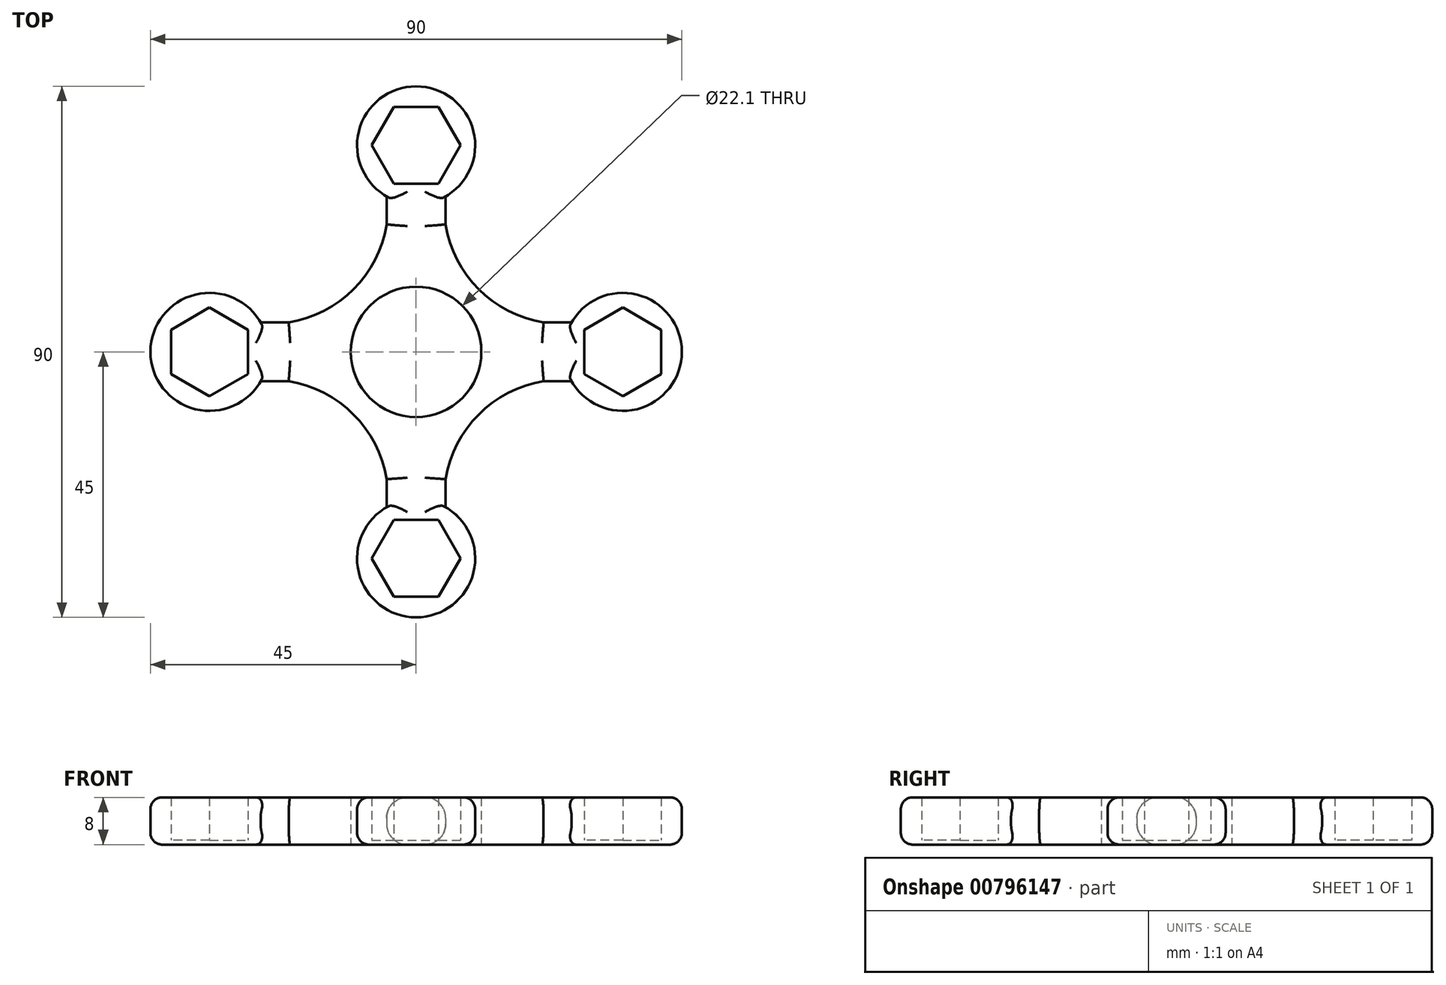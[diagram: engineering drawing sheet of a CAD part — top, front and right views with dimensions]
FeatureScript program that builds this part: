
annotation { "Feature Type Name" : "Feature", "Feature Type Description" : "" }
export const myFeature = defineFeature(function(context is Context, id is Id, definition is map)
    precondition{}
    {
        {
            var Q0;
            Q0=qCreatedBy(makeId("Top.planeOp"),FACE);
            var sketch = newSketch(context, id + "F0", { "sketchPlane" : qUnion([Q0])});
            skCircle(sketch, "E0", {"center": v(0, 0) * mm, "radius": 11.05 * mm});
            skCircle(sketch, "E1", {"center": v(0, 0) * mm, "radius": 35 * mm, "construction": true});
            skPoint(sketch, "E2", {"position": v(-35, 0) * mm});
            skPoint(sketch, "E3", {"position": v(35, 0) * mm});
            skPoint(sketch, "E4", {"position": v(0, 35) * mm});
            skPoint(sketch, "E5", {"position": v(0, -35) * mm});
            skCircle(sketch, "E6.cCircle", {"center": v(-35, 0) * mm, "radius": 6.5 * mm, "construction": true});
            skLineSegment(sketch, "E6.0", {"start": v(-28.5, 3.75) * mm, "end": v(-28.5, -3.75) * mm});
            skLineSegment(sketch, "E6.1", {"start": v(-28.5, -3.75) * mm, "end": v(-35, -7.5) * mm});
            skLineSegment(sketch, "E6.2", {"start": v(-35, -7.5) * mm, "end": v(-41.5, -3.75) * mm});
            skLineSegment(sketch, "E6.3", {"start": v(-41.5, -3.75) * mm, "end": v(-41.5, 3.75) * mm});
            skLineSegment(sketch, "E6.4", {"start": v(-41.5, 3.75) * mm, "end": v(-35, 7.5) * mm});
            skLineSegment(sketch, "E6.5", {"start": v(-35, 7.5) * mm, "end": v(-28.5, 3.75) * mm});
            skPoint(sketch, "E6.0.midPoint", {"position": v(-28.5, 0) * mm});
            skCircle(sketch, "E7.cCircle", {"center": v(35, 0) * mm, "radius": 6.5 * mm, "construction": true});
            skLineSegment(sketch, "E7.0", {"start": v(28.5, -3.75) * mm, "end": v(28.5, 3.75) * mm});
            skLineSegment(sketch, "E7.1", {"start": v(28.5, 3.75) * mm, "end": v(35, 7.5) * mm});
            skLineSegment(sketch, "E7.2", {"start": v(35, 7.5) * mm, "end": v(41.5, 3.75) * mm});
            skLineSegment(sketch, "E7.3", {"start": v(41.5, 3.75) * mm, "end": v(41.5, -3.75) * mm});
            skLineSegment(sketch, "E7.4", {"start": v(41.5, -3.75) * mm, "end": v(35, -7.5) * mm});
            skLineSegment(sketch, "E7.5", {"start": v(35, -7.5) * mm, "end": v(28.5, -3.75) * mm});
            skPoint(sketch, "E7.0.midPoint", {"position": v(28.5, 0) * mm});
            skCircle(sketch, "E8.cCircle", {"center": v(0, 35) * mm, "radius": 6.5 * mm, "construction": true});
            skLineSegment(sketch, "E8.0", {"start": v(3.75, 28.5) * mm, "end": v(-3.75, 28.5) * mm});
            skLineSegment(sketch, "E8.1", {"start": v(-3.75, 28.5) * mm, "end": v(-7.5, 35) * mm});
            skLineSegment(sketch, "E8.3", {"start": v(-3.75, 41.5) * mm, "end": v(3.75, 41.5) * mm});
            skLineSegment(sketch, "E8.4", {"start": v(3.75, 41.5) * mm, "end": v(7.5, 35) * mm});
            skLineSegment(sketch, "E8.5", {"start": v(7.5, 35) * mm, "end": v(3.75, 28.5) * mm});
            skPoint(sketch, "E8.0.midPoint", {"position": v(0, 28.5) * mm});
            skCircle(sketch, "E9.cCircle", {"center": v(0, -35) * mm, "radius": 6.5 * mm, "construction": true});
            skLineSegment(sketch, "E9.0", {"start": v(-3.75, -28.5) * mm, "end": v(3.75, -28.5) * mm});
            skLineSegment(sketch, "E9.1", {"start": v(3.75, -28.5) * mm, "end": v(7.5, -35) * mm});
            skLineSegment(sketch, "E9.2", {"start": v(7.5, -35) * mm, "end": v(3.75, -41.5) * mm});
            skLineSegment(sketch, "E9.3", {"start": v(3.75, -41.5) * mm, "end": v(-3.75, -41.5) * mm});
            skLineSegment(sketch, "E9.4", {"start": v(-3.75, -41.5) * mm, "end": v(-7.5, -35) * mm});
            skLineSegment(sketch, "E9.5", {"start": v(-7.5, -35) * mm, "end": v(-3.75, -28.5) * mm});
            skPoint(sketch, "E9.0.midPoint", {"position": v(0, -28.5) * mm});
            skCircle(sketch, "E10", {"center": v(0, 35) * mm, "radius": 10 * mm});
            skCircle(sketch, "E11", {"center": v(0, 0) * mm, "radius": 15 * mm});
            skLineSegment(sketch, "E12", {"start": v(0, 0) * mm, "end": v(-35, 0) * mm, "construction": true});
            skLineSegment(sketch, "E13", {"start": v(0, 0) * mm, "end": v(35, 0) * mm, "construction": true});
            skLineSegment(sketch, "E14", {"start": v(0, 0) * mm, "end": v(0, -35) * mm, "construction": true});
            skLineSegment(sketch, "E15", {"start": v(0, 0) * mm, "end": v(0, 35) * mm, "construction": true});
            skLineSegment(sketch, "E16.0", {"start": v(0, 5) * mm, "end": v(-30.5, 5) * mm});
            skLineSegment(sketch, "E17.0", {"start": v(0, -5) * mm, "end": v(30.5, -5) * mm});
            skLineSegment(sketch, "E18.0", {"start": v(0, 5) * mm, "end": v(30.5, 5) * mm});
            skLineSegment(sketch, "E19.0", {"start": v(0, -5) * mm, "end": v(-30.5, -5) * mm});
            skLineSegment(sketch, "E20.0", {"start": v(-5, 0) * mm, "end": v(-5, -30.5) * mm});
            skLineSegment(sketch, "E21.0", {"start": v(5, 0) * mm, "end": v(5, -30.5) * mm});
            skLineSegment(sketch, "E22.0", {"start": v(5, 0) * mm, "end": v(5, 30.5) * mm});
            skLineSegment(sketch, "E23.0", {"start": v(-5, 0) * mm, "end": v(-5, 30.5) * mm});
            skLineSegment(sketch, "E24", {"start": v(-7.5, 35) * mm, "end": v(-3.75, 41.5) * mm});
            skCircle(sketch, "E25", {"center": v(-35, 0) * mm, "radius": 10 * mm});
            skCircle(sketch, "E26", {"center": v(0, -35) * mm, "radius": 10 * mm});
            skCircle(sketch, "E27", {"center": v(35, 0) * mm, "radius": 10 * mm});
            skLineSegment(sketch, "E28", {"start": v(0, 0) * mm, "end": v(-24.75, 24.75) * mm, "construction": true});
            skLineSegment(sketch, "E29", {"start": v(24.75, -24.75) * mm, "end": v(0, 0) * mm, "construction": true});
            skLineSegment(sketch, "E30", {"start": v(24.75, 24.75) * mm, "end": v(0, 0) * mm, "construction": true});
            skLineSegment(sketch, "E31", {"start": v(-24.75, -24.75) * mm, "end": v(0, 0) * mm, "construction": true});
            skCircle(sketch, "E32", {"center": v(-24.75, 24.75) * mm, "radius": 20 * mm});
            skCircle(sketch, "E33", {"center": v(24.75, 24.75) * mm, "radius": 20 * mm});
            skCircle(sketch, "E34", {"center": v(24.75, -24.75) * mm, "radius": 20 * mm});
            skCircle(sketch, "E35", {"center": v(-24.75, -24.75) * mm, "radius": 20 * mm});
            skSolve(sketch);
        }
        {
            var Q0;
            Q0=makeQuery(id+"F0.imprint","IMPRINT",FACE,{"disambiguationData":[TD([[makeQuery(id+"F0.imprint","IMPRINT",EDGE,{"derivedFrom":sQuery(id+"F0.wireOp",EDGE,"E6.0")}),1.0]])]});
            var Q1;
            {var subQ0=sQuery(id+"F0.wireOp",EDGE,"E23.0");var subQ1=sQuery(id+"F0.wireOp",EDGE,"E0");var subQ2=makeQuery(id+"F0.imprint","INTERSECT",VERTEX,{"derivedFrom":[subQ1,subQ0]});Q1=makeQuery(id+"F0.imprint","IMPRINT",FACE,{"disambiguationData":[TD([[makeQuery(id+"F0.imprint","IMPRINT",EDGE,{"disambiguationData":[TD([[subQ2,-1.0]])],"derivedFrom":subQ1}),-1.0]])]});}
            var Q2;
            {var subQ0=sQuery(id+"F0.wireOp",EDGE,"E22.0");var subQ1=sQuery(id+"F0.wireOp",EDGE,"E0");var subQ2=makeQuery(id+"F0.imprint","INTERSECT",VERTEX,{"derivedFrom":[subQ1,subQ0]});Q2=makeQuery(id+"F0.imprint","IMPRINT",FACE,{"disambiguationData":[TD([[makeQuery(id+"F0.imprint","IMPRINT",EDGE,{"disambiguationData":[TD([[subQ2,-1.0]])],"derivedFrom":subQ1}),-1.0]])]});}
            var Q3;
            {var subQ0=sQuery(id+"F0.wireOp",EDGE,"E22.0");var subQ1=sQuery(id+"F0.wireOp",EDGE,"E0");var subQ2=makeQuery(id+"F0.imprint","INTERSECT",VERTEX,{"derivedFrom":[subQ1,subQ0]});Q3=makeQuery(id+"F0.imprint","IMPRINT",FACE,{"disambiguationData":[TD([[makeQuery(id+"F0.imprint","IMPRINT",EDGE,{"disambiguationData":[TD([[subQ2,1.0]])],"derivedFrom":subQ1}),-1.0]])]});}
            var Q4;
            {var subQ0=sQuery(id+"F0.wireOp",EDGE,"E18.0");var subQ1=sQuery(id+"F0.wireOp",EDGE,"E0");var subQ2=makeQuery(id+"F0.imprint","INTERSECT",VERTEX,{"derivedFrom":[subQ1,subQ0]});Q4=makeQuery(id+"F0.imprint","IMPRINT",FACE,{"disambiguationData":[TD([[makeQuery(id+"F0.imprint","IMPRINT",EDGE,{"disambiguationData":[TD([[subQ2,1.0]])],"derivedFrom":subQ1}),-1.0]])]});}
            var Q5;
            {var subQ0=sQuery(id+"F0.wireOp",EDGE,"E21.0");var subQ1=sQuery(id+"F0.wireOp",EDGE,"E0");var subQ2=makeQuery(id+"F0.imprint","INTERSECT",VERTEX,{"derivedFrom":[subQ1,subQ0]});Q5=makeQuery(id+"F0.imprint","IMPRINT",FACE,{"disambiguationData":[TD([[makeQuery(id+"F0.imprint","IMPRINT",EDGE,{"disambiguationData":[TD([[subQ2,-1.0]])],"derivedFrom":subQ1}),-1.0]])]});}
            var Q6;
            {var subQ0=sQuery(id+"F0.wireOp",EDGE,"E20.0");var subQ1=sQuery(id+"F0.wireOp",EDGE,"E0");var subQ2=makeQuery(id+"F0.imprint","INTERSECT",VERTEX,{"derivedFrom":[subQ1,subQ0]});Q6=makeQuery(id+"F0.imprint","IMPRINT",FACE,{"disambiguationData":[TD([[makeQuery(id+"F0.imprint","IMPRINT",EDGE,{"disambiguationData":[TD([[subQ2,-1.0]])],"derivedFrom":subQ1}),-1.0]])]});}
            var Q7;
            {var subQ0=sQuery(id+"F0.wireOp",EDGE,"E19.0");var subQ1=sQuery(id+"F0.wireOp",EDGE,"E0");var subQ2=makeQuery(id+"F0.imprint","INTERSECT",VERTEX,{"derivedFrom":[subQ1,subQ0]});Q7=makeQuery(id+"F0.imprint","IMPRINT",FACE,{"disambiguationData":[TD([[makeQuery(id+"F0.imprint","IMPRINT",EDGE,{"disambiguationData":[TD([[subQ2,-1.0]])],"derivedFrom":subQ1}),-1.0]])]});}
            var Q8;
            {var subQ0=sQuery(id+"F0.wireOp",EDGE,"E20.0");var subQ1=sQuery(id+"F0.wireOp",EDGE,"E11");var subQ2=makeQuery(id+"F0.imprint","INTERSECT",VERTEX,{"derivedFrom":[subQ1,subQ0]});Q8=makeQuery(id+"F0.imprint","IMPRINT",FACE,{"disambiguationData":[TD([[makeQuery(id+"F0.imprint","IMPRINT",EDGE,{"disambiguationData":[TD([[subQ2,-1.0]])],"derivedFrom":subQ1}),-1.0]])]});}
            var Q9;
            {var subQ0=sQuery(id+"F0.wireOp",EDGE,"E16.0");var subQ1=sQuery(id+"F0.wireOp",EDGE,"E11");var subQ2=makeQuery(id+"F0.imprint","INTERSECT",VERTEX,{"derivedFrom":[subQ1,subQ0]});Q9=makeQuery(id+"F0.imprint","IMPRINT",FACE,{"disambiguationData":[TD([[makeQuery(id+"F0.imprint","IMPRINT",EDGE,{"disambiguationData":[TD([[subQ2,-1.0]])],"derivedFrom":subQ1}),-1.0]])]});}
            var Q10;
            {var subQ0=sQuery(id+"F0.wireOp",EDGE,"E18.0");var subQ1=sQuery(id+"F0.wireOp",EDGE,"E11");var subQ2=makeQuery(id+"F0.imprint","INTERSECT",VERTEX,{"derivedFrom":[subQ1,subQ0]});Q10=makeQuery(id+"F0.imprint","IMPRINT",FACE,{"disambiguationData":[TD([[makeQuery(id+"F0.imprint","IMPRINT",EDGE,{"disambiguationData":[TD([[subQ2,1.0]])],"derivedFrom":subQ1}),-1.0]])]});}
            var Q11;
            {var subQ0=sQuery(id+"F0.wireOp",EDGE,"E16.0");var subQ1=sQuery(id+"F0.wireOp",EDGE,"E0");var subQ2=makeQuery(id+"F0.imprint","INTERSECT",VERTEX,{"derivedFrom":[subQ1,subQ0]});Q11=makeQuery(id+"F0.imprint","IMPRINT",FACE,{"disambiguationData":[TD([[makeQuery(id+"F0.imprint","IMPRINT",EDGE,{"disambiguationData":[TD([[subQ2,-1.0]])],"derivedFrom":subQ1}),-1.0]])]});}
            var Q12;
            {var subQ0=sQuery(id+"F0.wireOp",EDGE,"E22.0");var subQ1=sQuery(id+"F0.wireOp",EDGE,"E10");var subQ2=makeQuery(id+"F0.imprint","INTERSECT",VERTEX,{"derivedFrom":[subQ1,subQ0]});Q12=makeQuery(id+"F0.imprint","IMPRINT",FACE,{"disambiguationData":[TD([[makeQuery(id+"F0.imprint","IMPRINT",EDGE,{"disambiguationData":[TD([[subQ2,1.0]])],"derivedFrom":subQ1}),-1.0]])]});}
            var Q13;
            Q13=makeQuery(id+"F0.imprint","IMPRINT",FACE,{"disambiguationData":[TD([[makeQuery(id+"F0.imprint","IMPRINT",EDGE,{"derivedFrom":sQuery(id+"F0.wireOp",EDGE,"E8.0")}),1.0]])]});
            var Q14;
            Q14=makeQuery(id+"F0.imprint","IMPRINT",FACE,{"disambiguationData":[TD([[makeQuery(id+"F0.imprint","IMPRINT",EDGE,{"derivedFrom":sQuery(id+"F0.wireOp",EDGE,"E7.0")}),1.0]])]});
            var Q15;
            {var subQ0=sQuery(id+"F0.wireOp",EDGE,"E32");var subQ1=sQuery(id+"F0.wireOp",EDGE,"E16.0");var subQ2=makeQuery(id+"F0.imprint","INTERSECT",VERTEX,{"disambiguationData":[OD(0.0)],"derivedFrom":[subQ1,subQ0]});Q15=makeQuery(id+"F0.imprint","IMPRINT",FACE,{"disambiguationData":[TD([[makeQuery(id+"F0.imprint","IMPRINT",EDGE,{"disambiguationData":[TD([[subQ2,1.0]])],"derivedFrom":subQ1}),-1.0]])]});}
            var Q16;
            {var subQ0=sQuery(id+"F0.wireOp",EDGE,"E32");var subQ1=sQuery(id+"F0.wireOp",EDGE,"E11");var subQ2=makeQuery(id+"F0.imprint","INTERSECT",VERTEX,{"derivedFrom":[subQ1,subQ0]});Q16=makeQuery(id+"F0.imprint","IMPRINT",FACE,{"disambiguationData":[TD([[makeQuery(id+"F0.imprint","IMPRINT",EDGE,{"disambiguationData":[TD([[subQ2,-1.0]])],"derivedFrom":subQ1}),-1.0]])]});}
            var Q17;
            {var subQ0=sQuery(id+"F0.wireOp",EDGE,"E23.0");var subQ1=sQuery(id+"F0.wireOp",EDGE,"E11");var subQ2=makeQuery(id+"F0.imprint","INTERSECT",VERTEX,{"derivedFrom":[subQ1,subQ0]});Q17=makeQuery(id+"F0.imprint","IMPRINT",FACE,{"disambiguationData":[TD([[makeQuery(id+"F0.imprint","IMPRINT",EDGE,{"disambiguationData":[TD([[subQ2,-1.0]])],"derivedFrom":subQ1}),-1.0]])]});}
            var Q18;
            {var subQ0=sQuery(id+"F0.wireOp",EDGE,"E32");var subQ1=sQuery(id+"F0.wireOp",EDGE,"E10");var subQ2=makeQuery(id+"F0.imprint","INTERSECT",VERTEX,{"disambiguationData":[OD(0.0)],"derivedFrom":[subQ1,subQ0]});Q18=makeQuery(id+"F0.imprint","IMPRINT",FACE,{"disambiguationData":[TD([[makeQuery(id+"F0.imprint","IMPRINT",EDGE,{"disambiguationData":[TD([[subQ2,-1.0]])],"derivedFrom":subQ1}),1.0]])]});}
            var Q19;
            {var subQ0=sQuery(id+"F0.wireOp",EDGE,"E33");var subQ1=sQuery(id+"F0.wireOp",EDGE,"E10");var subQ2=makeQuery(id+"F0.imprint","INTERSECT",VERTEX,{"disambiguationData":[OD(0.0)],"derivedFrom":[subQ1,subQ0]});Q19=makeQuery(id+"F0.imprint","IMPRINT",FACE,{"disambiguationData":[TD([[makeQuery(id+"F0.imprint","IMPRINT",EDGE,{"disambiguationData":[TD([[subQ2,1.0]])],"derivedFrom":subQ1}),1.0]])]});}
            var Q20;
            {var subQ0=sQuery(id+"F0.wireOp",EDGE,"E33");var subQ1=sQuery(id+"F0.wireOp",EDGE,"E11");var subQ2=makeQuery(id+"F0.imprint","INTERSECT",VERTEX,{"derivedFrom":[subQ1,subQ0]});Q20=makeQuery(id+"F0.imprint","IMPRINT",FACE,{"disambiguationData":[TD([[makeQuery(id+"F0.imprint","IMPRINT",EDGE,{"disambiguationData":[TD([[subQ2,-1.0]])],"derivedFrom":subQ1}),-1.0]])]});}
            var Q21;
            {var subQ0=sQuery(id+"F0.wireOp",EDGE,"E33");var subQ1=sQuery(id+"F0.wireOp",EDGE,"E11");var subQ2=makeQuery(id+"F0.imprint","INTERSECT",VERTEX,{"derivedFrom":[subQ1,subQ0]});Q21=makeQuery(id+"F0.imprint","IMPRINT",FACE,{"disambiguationData":[TD([[makeQuery(id+"F0.imprint","IMPRINT",EDGE,{"disambiguationData":[TD([[subQ2,1.0]])],"derivedFrom":subQ1}),-1.0]])]});}
            var Q22;
            {var subQ0=sQuery(id+"F0.wireOp",EDGE,"E34");var subQ1=sQuery(id+"F0.wireOp",EDGE,"E11");var subQ2=makeQuery(id+"F0.imprint","INTERSECT",VERTEX,{"derivedFrom":[subQ1,subQ0]});Q22=makeQuery(id+"F0.imprint","IMPRINT",FACE,{"disambiguationData":[TD([[makeQuery(id+"F0.imprint","IMPRINT",EDGE,{"disambiguationData":[TD([[subQ2,-1.0]])],"derivedFrom":subQ1}),-1.0]])]});}
            var Q23;
            {var subQ0=sQuery(id+"F0.wireOp",EDGE,"E34");var subQ1=sQuery(id+"F0.wireOp",EDGE,"E17.0");var subQ2=makeQuery(id+"F0.imprint","INTERSECT",VERTEX,{"disambiguationData":[OD(0.0)],"derivedFrom":[subQ1,subQ0]});Q23=makeQuery(id+"F0.imprint","IMPRINT",FACE,{"disambiguationData":[TD([[makeQuery(id+"F0.imprint","IMPRINT",EDGE,{"disambiguationData":[TD([[subQ2,1.0]])],"derivedFrom":subQ1}),-1.0]])]});}
            var Q24;
            {var subQ0=sQuery(id+"F0.wireOp",EDGE,"E33");var subQ1=sQuery(id+"F0.wireOp",EDGE,"E18.0");var subQ2=makeQuery(id+"F0.imprint","INTERSECT",VERTEX,{"disambiguationData":[OD(0.0)],"derivedFrom":[subQ1,subQ0]});Q24=makeQuery(id+"F0.imprint","IMPRINT",FACE,{"disambiguationData":[TD([[makeQuery(id+"F0.imprint","IMPRINT",EDGE,{"disambiguationData":[TD([[subQ2,1.0]])],"derivedFrom":subQ1}),1.0]])]});}
            var Q25;
            {var subQ0=sQuery(id+"F0.wireOp",EDGE,"E34");var subQ1=sQuery(id+"F0.wireOp",EDGE,"E21.0");var subQ2=makeQuery(id+"F0.imprint","INTERSECT",VERTEX,{"disambiguationData":[OD(0.0)],"derivedFrom":[subQ1,subQ0]});Q25=makeQuery(id+"F0.imprint","IMPRINT",FACE,{"disambiguationData":[TD([[makeQuery(id+"F0.imprint","IMPRINT",EDGE,{"disambiguationData":[TD([[subQ2,1.0]])],"derivedFrom":subQ1}),1.0]])]});}
            var Q26;
            {var subQ0=sQuery(id+"F0.wireOp",EDGE,"E21.0");var subQ1=sQuery(id+"F0.wireOp",EDGE,"E11");var subQ2=makeQuery(id+"F0.imprint","INTERSECT",VERTEX,{"derivedFrom":[subQ1,subQ0]});Q26=makeQuery(id+"F0.imprint","IMPRINT",FACE,{"disambiguationData":[TD([[makeQuery(id+"F0.imprint","IMPRINT",EDGE,{"disambiguationData":[TD([[subQ2,-1.0]])],"derivedFrom":subQ1}),-1.0]])]});}
            var Q27;
            {var subQ0=sQuery(id+"F0.wireOp",EDGE,"E35");var subQ1=sQuery(id+"F0.wireOp",EDGE,"E11");var subQ2=makeQuery(id+"F0.imprint","INTERSECT",VERTEX,{"derivedFrom":[subQ1,subQ0]});Q27=makeQuery(id+"F0.imprint","IMPRINT",FACE,{"disambiguationData":[TD([[makeQuery(id+"F0.imprint","IMPRINT",EDGE,{"disambiguationData":[TD([[subQ2,-1.0]])],"derivedFrom":subQ1}),-1.0]])]});}
            var Q28;
            {var subQ0=sQuery(id+"F0.wireOp",EDGE,"E19.0");var subQ1=sQuery(id+"F0.wireOp",EDGE,"E11");var subQ2=makeQuery(id+"F0.imprint","INTERSECT",VERTEX,{"derivedFrom":[subQ1,subQ0]});Q28=makeQuery(id+"F0.imprint","IMPRINT",FACE,{"disambiguationData":[TD([[makeQuery(id+"F0.imprint","IMPRINT",EDGE,{"disambiguationData":[TD([[subQ2,-1.0]])],"derivedFrom":subQ1}),-1.0]])]});}
            var Q29;
            {var subQ0=sQuery(id+"F0.wireOp",EDGE,"E35");var subQ1=sQuery(id+"F0.wireOp",EDGE,"E19.0");var subQ2=makeQuery(id+"F0.imprint","INTERSECT",VERTEX,{"disambiguationData":[OD(0.0)],"derivedFrom":[subQ1,subQ0]});Q29=makeQuery(id+"F0.imprint","IMPRINT",FACE,{"disambiguationData":[TD([[makeQuery(id+"F0.imprint","IMPRINT",EDGE,{"disambiguationData":[TD([[subQ2,1.0]])],"derivedFrom":subQ1}),1.0]])]});}
            var Q30;
            {var subQ0=sQuery(id+"F0.wireOp",EDGE,"E35");var subQ1=sQuery(id+"F0.wireOp",EDGE,"E19.0");var subQ2=makeQuery(id+"F0.imprint","INTERSECT",VERTEX,{"disambiguationData":[OD(1.0)],"derivedFrom":[subQ1,subQ0]});Q30=makeQuery(id+"F0.imprint","IMPRINT",FACE,{"disambiguationData":[TD([[makeQuery(id+"F0.imprint","IMPRINT",EDGE,{"disambiguationData":[TD([[subQ2,-1.0]])],"derivedFrom":subQ1}),-1.0]])]});}
            var Q31;
            {var subQ0=sQuery(id+"F0.wireOp",EDGE,"E35");var subQ1=sQuery(id+"F0.wireOp",EDGE,"E19.0");var subQ2=makeQuery(id+"F0.imprint","INTERSECT",VERTEX,{"disambiguationData":[OD(0.0)],"derivedFrom":[subQ1,subQ0]});Q31=makeQuery(id+"F0.imprint","IMPRINT",FACE,{"disambiguationData":[TD([[makeQuery(id+"F0.imprint","IMPRINT",EDGE,{"disambiguationData":[TD([[subQ2,1.0]])],"derivedFrom":subQ1}),-1.0]])]});}
            var Q32;
            {var subQ0=sQuery(id+"F0.wireOp",EDGE,"E32");var subQ1=sQuery(id+"F0.wireOp",EDGE,"E16.0");var subQ2=makeQuery(id+"F0.imprint","INTERSECT",VERTEX,{"disambiguationData":[OD(0.0)],"derivedFrom":[subQ1,subQ0]});Q32=makeQuery(id+"F0.imprint","IMPRINT",FACE,{"disambiguationData":[TD([[makeQuery(id+"F0.imprint","IMPRINT",EDGE,{"disambiguationData":[TD([[subQ2,1.0]])],"derivedFrom":subQ1}),1.0]])]});}
            var Q33;
            {var subQ0=sQuery(id+"F0.wireOp",EDGE,"E32");var subQ1=sQuery(id+"F0.wireOp",EDGE,"E16.0");var subQ2=makeQuery(id+"F0.imprint","INTERSECT",VERTEX,{"disambiguationData":[OD(1.0)],"derivedFrom":[subQ1,subQ0]});Q33=makeQuery(id+"F0.imprint","IMPRINT",FACE,{"disambiguationData":[TD([[makeQuery(id+"F0.imprint","IMPRINT",EDGE,{"disambiguationData":[TD([[subQ2,-1.0]])],"derivedFrom":subQ1}),1.0]])]});}
            var Q34;
            {var subQ0=sQuery(id+"F0.wireOp",EDGE,"E23.0");var subQ1=sQuery(id+"F0.wireOp",EDGE,"E10");var subQ2=makeQuery(id+"F0.imprint","INTERSECT",VERTEX,{"derivedFrom":[subQ1,subQ0]});Q34=makeQuery(id+"F0.imprint","IMPRINT",FACE,{"disambiguationData":[TD([[makeQuery(id+"F0.imprint","IMPRINT",EDGE,{"disambiguationData":[TD([[subQ2,-1.0]])],"derivedFrom":subQ1}),1.0]])]});}
            var Q35;
            {var subQ0=sQuery(id+"F0.wireOp",EDGE,"E23.0");var subQ1=sQuery(id+"F0.wireOp",EDGE,"E10");var subQ2=makeQuery(id+"F0.imprint","INTERSECT",VERTEX,{"derivedFrom":[subQ1,subQ0]});Q35=makeQuery(id+"F0.imprint","IMPRINT",FACE,{"disambiguationData":[TD([[makeQuery(id+"F0.imprint","IMPRINT",EDGE,{"disambiguationData":[TD([[subQ2,-1.0]])],"derivedFrom":subQ1}),-1.0]])]});}
            var Q36;
            {var subQ0=sQuery(id+"F0.wireOp",EDGE,"E33");var subQ1=sQuery(id+"F0.wireOp",EDGE,"E10");var subQ2=makeQuery(id+"F0.imprint","INTERSECT",VERTEX,{"disambiguationData":[OD(1.0)],"derivedFrom":[subQ1,subQ0]});Q36=makeQuery(id+"F0.imprint","IMPRINT",FACE,{"disambiguationData":[TD([[makeQuery(id+"F0.imprint","IMPRINT",EDGE,{"disambiguationData":[TD([[subQ2,-1.0]])],"derivedFrom":subQ1}),1.0]])]});}
            var Q37;
            {var subQ7=sQuery(id+"F0.wireOp",EDGE,"E32");var subQ9=sQuery(id+"F0.wireOp",EDGE,"E10");var subQ11=makeQuery(id+"F0.imprint","INTERSECT",VERTEX,{"disambiguationData":[OD(1.0)],"derivedFrom":[subQ9,subQ7]});Q37=makeQuery(id+"F0.imprint","IMPRINT",FACE,{"disambiguationData":[TD([[makeQuery(id+"F0.imprint","IMPRINT",EDGE,{"disambiguationData":[TD([[subQ11,-1.0]])],"derivedFrom":subQ9}),-1.0]])]});}
            var Q38;
            {var subQ0=sQuery(id+"F0.wireOp",EDGE,"E33");var subQ1=sQuery(id+"F0.wireOp",EDGE,"E18.0");var subQ2=makeQuery(id+"F0.imprint","INTERSECT",VERTEX,{"disambiguationData":[OD(1.0)],"derivedFrom":[subQ1,subQ0]});Q38=makeQuery(id+"F0.imprint","IMPRINT",FACE,{"disambiguationData":[TD([[makeQuery(id+"F0.imprint","IMPRINT",EDGE,{"disambiguationData":[TD([[subQ2,-1.0]])],"derivedFrom":subQ1}),-1.0]])]});}
            var Q39;
            {var subQ0=sQuery(id+"F0.wireOp",EDGE,"E33");var subQ1=sQuery(id+"F0.wireOp",EDGE,"E18.0");var subQ2=makeQuery(id+"F0.imprint","INTERSECT",VERTEX,{"disambiguationData":[OD(0.0)],"derivedFrom":[subQ1,subQ0]});Q39=makeQuery(id+"F0.imprint","IMPRINT",FACE,{"disambiguationData":[TD([[makeQuery(id+"F0.imprint","IMPRINT",EDGE,{"disambiguationData":[TD([[subQ2,1.0]])],"derivedFrom":subQ1}),-1.0]])]});}
            var Q40;
            {var subQ0=sQuery(id+"F0.wireOp",EDGE,"E34");var subQ1=sQuery(id+"F0.wireOp",EDGE,"E17.0");var subQ2=makeQuery(id+"F0.imprint","INTERSECT",VERTEX,{"disambiguationData":[OD(1.0)],"derivedFrom":[subQ1,subQ0]});Q40=makeQuery(id+"F0.imprint","IMPRINT",FACE,{"disambiguationData":[TD([[makeQuery(id+"F0.imprint","IMPRINT",EDGE,{"disambiguationData":[TD([[subQ2,-1.0]])],"derivedFrom":subQ1}),1.0]])]});}
            var Q41;
            {var subQ0=sQuery(id+"F0.wireOp",EDGE,"E34");var subQ1=sQuery(id+"F0.wireOp",EDGE,"E17.0");var subQ2=makeQuery(id+"F0.imprint","INTERSECT",VERTEX,{"disambiguationData":[OD(0.0)],"derivedFrom":[subQ1,subQ0]});Q41=makeQuery(id+"F0.imprint","IMPRINT",FACE,{"disambiguationData":[TD([[makeQuery(id+"F0.imprint","IMPRINT",EDGE,{"disambiguationData":[TD([[subQ2,1.0]])],"derivedFrom":subQ1}),1.0]])]});}
            var Q42;
            {var subQ0=sQuery(id+"F0.wireOp",EDGE,"E35");var subQ1=sQuery(id+"F0.wireOp",EDGE,"E20.0");var subQ2=makeQuery(id+"F0.imprint","INTERSECT",VERTEX,{"disambiguationData":[OD(1.0)],"derivedFrom":[subQ1,subQ0]});Q42=makeQuery(id+"F0.imprint","IMPRINT",FACE,{"disambiguationData":[TD([[makeQuery(id+"F0.imprint","IMPRINT",EDGE,{"disambiguationData":[TD([[subQ2,-1.0]])],"derivedFrom":subQ1}),1.0]])]});}
            var Q43;
            {var subQ0=sQuery(id+"F0.wireOp",EDGE,"E34");var subQ1=sQuery(id+"F0.wireOp",EDGE,"E21.0");var subQ2=makeQuery(id+"F0.imprint","INTERSECT",VERTEX,{"disambiguationData":[OD(1.0)],"derivedFrom":[subQ1,subQ0]});Q43=makeQuery(id+"F0.imprint","IMPRINT",FACE,{"disambiguationData":[TD([[makeQuery(id+"F0.imprint","IMPRINT",EDGE,{"disambiguationData":[TD([[subQ2,-1.0]])],"derivedFrom":subQ1}),-1.0]])]});}
            var Q44;
            {var subQ0=sQuery(id+"F0.wireOp",EDGE,"E34");var subQ1=sQuery(id+"F0.wireOp",EDGE,"E21.0");var subQ2=makeQuery(id+"F0.imprint","INTERSECT",VERTEX,{"disambiguationData":[OD(0.0)],"derivedFrom":[subQ1,subQ0]});Q44=makeQuery(id+"F0.imprint","IMPRINT",FACE,{"disambiguationData":[TD([[makeQuery(id+"F0.imprint","IMPRINT",EDGE,{"disambiguationData":[TD([[subQ2,1.0]])],"derivedFrom":subQ1}),-1.0]])]});}
            var Q45;
            {var subQ0=sQuery(id+"F0.wireOp",EDGE,"E35");var subQ1=sQuery(id+"F0.wireOp",EDGE,"E20.0");var subQ2=makeQuery(id+"F0.imprint","INTERSECT",VERTEX,{"disambiguationData":[OD(0.0)],"derivedFrom":[subQ1,subQ0]});Q45=makeQuery(id+"F0.imprint","IMPRINT",FACE,{"disambiguationData":[TD([[makeQuery(id+"F0.imprint","IMPRINT",EDGE,{"disambiguationData":[TD([[subQ2,1.0]])],"derivedFrom":subQ1}),-1.0]])]});}
            var Q46;
            Q46=makeQuery(id+"F0.imprint","IMPRINT",FACE,{"disambiguationData":[TD([[makeQuery(id+"F0.imprint","IMPRINT",EDGE,{"derivedFrom":sQuery(id+"F0.wireOp",EDGE,"E9.0")}),1.0]])]});
            var Q47;
            {var subQ0=sQuery(id+"F0.wireOp",EDGE,"E35");var subQ1=sQuery(id+"F0.wireOp",EDGE,"E20.0");var subQ2=makeQuery(id+"F0.imprint","INTERSECT",VERTEX,{"disambiguationData":[OD(0.0)],"derivedFrom":[subQ1,subQ0]});Q47=makeQuery(id+"F0.imprint","IMPRINT",FACE,{"disambiguationData":[TD([[makeQuery(id+"F0.imprint","IMPRINT",EDGE,{"disambiguationData":[TD([[subQ2,1.0]])],"derivedFrom":subQ1}),1.0]])]});}
            extrude(context, id + "F1", {"entities" : qUnion([Q0, Q1, Q2, Q3, Q4, Q5, Q6, Q7, Q8, Q9, Q10, Q11, Q12, Q13, Q14, Q15, Q16, Q17, Q18, Q19, Q20, Q21, Q22, Q23, Q24, Q25, Q26, Q27, Q28, Q29, Q30, Q31, Q32, Q33, Q34, Q35, Q36, Q37, Q38, Q39, Q40, Q41, Q42, Q43, Q44, Q45, Q46, Q47]), "depth" : 8 * mm, "offsetDistance" : 25 * mm});
        }
        {
            var Q0;
            Q0=makeQuery(id+"F0.imprint","IMPRINT",FACE,{"disambiguationData":[TD([[makeQuery(id+"F0.imprint","IMPRINT",EDGE,{"derivedFrom":sQuery(id+"F0.wireOp",EDGE,"E6.0")}),-1.0]])]});
            var Q1;
            Q1=makeQuery(id+"F0.imprint","IMPRINT",FACE,{"disambiguationData":[TD([[makeQuery(id+"F0.imprint","IMPRINT",EDGE,{"derivedFrom":sQuery(id+"F0.wireOp",EDGE,"E9.0")}),-1.0]])]});
            var Q2;
            Q2=makeQuery(id+"F0.imprint","IMPRINT",FACE,{"disambiguationData":[TD([[makeQuery(id+"F0.imprint","IMPRINT",EDGE,{"derivedFrom":sQuery(id+"F0.wireOp",EDGE,"E8.0")}),-1.0]])]});
            var Q3;
            Q3=makeQuery(id+"F0.imprint","IMPRINT",FACE,{"disambiguationData":[TD([[makeQuery(id+"F0.imprint","IMPRINT",EDGE,{"derivedFrom":sQuery(id+"F0.wireOp",EDGE,"E7.0")}),-1.0]])]});
            extrude(context, id + "F2", {"entities" : qUnion([Q0, Q1, Q2, Q3]), "operationType" : NewBodyOperationType.ADD, "depth" : 0.75 * mm, "offsetDistance" : 25 * mm});
        }
        {
            var Q0;
            Q0=makeQuery(id+"F1.opExtrude","CAP_EDGE",EDGE,{"disambiguationData":[OSD([sQuery(id+"F0.wireOp",EDGE,"E19.0")])],"isStart":false});
            var Q1;
            Q1=makeQuery(id+"F1.opExtrude","CAP_EDGE",EDGE,{"disambiguationData":[OSD([sQuery(id+"F0.wireOp",EDGE,"E35")])],"isStart":false});
            var Q2;
            Q2=makeQuery(id+"F1.opExtrude","CAP_EDGE",EDGE,{"disambiguationData":[OSD([sQuery(id+"F0.wireOp",EDGE,"E20.0")])],"isStart":false});
            var Q3;
            Q3=makeQuery(id+"F1.opExtrude","CAP_EDGE",EDGE,{"disambiguationData":[OSD([sQuery(id+"F0.wireOp",EDGE,"E21.0")])],"isStart":false});
            var Q4;
            Q4=makeQuery(id+"F1.opExtrude","CAP_EDGE",EDGE,{"disambiguationData":[OSD([sQuery(id+"F0.wireOp",EDGE,"E34")])],"isStart":false});
            var Q5;
            Q5=makeQuery(id+"F1.opExtrude","CAP_EDGE",EDGE,{"disambiguationData":[OSD([sQuery(id+"F0.wireOp",EDGE,"E17.0")])],"isStart":false});
            var Q6;
            Q6=makeQuery(id+"F1.opExtrude","CAP_EDGE",EDGE,{"disambiguationData":[OSD([sQuery(id+"F0.wireOp",EDGE,"E18.0")])],"isStart":false});
            var Q7;
            Q7=makeQuery(id+"F1.opExtrude","CAP_EDGE",EDGE,{"disambiguationData":[OSD([sQuery(id+"F0.wireOp",EDGE,"E33")])],"isStart":false});
            var Q8;
            Q8=makeQuery(id+"F1.opExtrude","CAP_EDGE",EDGE,{"disambiguationData":[OSD([sQuery(id+"F0.wireOp",EDGE,"E22.0")])],"isStart":false});
            var Q9;
            Q9=makeQuery(id+"F1.opExtrude","CAP_EDGE",EDGE,{"disambiguationData":[OSD([sQuery(id+"F0.wireOp",EDGE,"E23.0")])],"isStart":false});
            var Q10;
            Q10=makeQuery(id+"F1.opExtrude","CAP_EDGE",EDGE,{"disambiguationData":[OSD([sQuery(id+"F0.wireOp",EDGE,"E32")])],"isStart":false});
            var Q11;
            Q11=makeQuery(id+"F1.opExtrude","CAP_EDGE",EDGE,{"disambiguationData":[OSD([sQuery(id+"F0.wireOp",EDGE,"E16.0")])],"isStart":false});
            var Q12;
            Q12=makeQuery(id+"F1.opExtrude","CAP_EDGE",EDGE,{"disambiguationData":[OSD([sQuery(id+"F0.wireOp",EDGE,"E35")])],"isStart":true});
            var Q13;
            Q13=makeQuery(id+"F1.opExtrude","CAP_EDGE",EDGE,{"disambiguationData":[OSD([sQuery(id+"F0.wireOp",EDGE,"E19.0")])],"isStart":true});
            var Q14;
            Q14=makeQuery(id+"F1.opExtrude","CAP_EDGE",EDGE,{"disambiguationData":[OSD([sQuery(id+"F0.wireOp",EDGE,"E20.0")])],"isStart":true});
            var Q15;
            Q15=makeQuery(id+"F1.opExtrude","CAP_EDGE",EDGE,{"disambiguationData":[OSD([sQuery(id+"F0.wireOp",EDGE,"E34")])],"isStart":true});
            var Q16;
            Q16=makeQuery(id+"F1.opExtrude","CAP_EDGE",EDGE,{"disambiguationData":[OSD([sQuery(id+"F0.wireOp",EDGE,"E21.0")])],"isStart":true});
            var Q17;
            Q17=makeQuery(id+"F1.opExtrude","CAP_EDGE",EDGE,{"disambiguationData":[OSD([sQuery(id+"F0.wireOp",EDGE,"E17.0")])],"isStart":true});
            var Q18;
            Q18=makeQuery(id+"F1.opExtrude","CAP_EDGE",EDGE,{"disambiguationData":[OSD([sQuery(id+"F0.wireOp",EDGE,"E33")])],"isStart":true});
            var Q19;
            Q19=makeQuery(id+"F1.opExtrude","CAP_EDGE",EDGE,{"disambiguationData":[OSD([sQuery(id+"F0.wireOp",EDGE,"E18.0")])],"isStart":true});
            var Q20;
            Q20=makeQuery(id+"F1.opExtrude","CAP_EDGE",EDGE,{"disambiguationData":[OSD([sQuery(id+"F0.wireOp",EDGE,"E22.0")])],"isStart":true});
            var Q21;
            Q21=makeQuery(id+"F1.opExtrude","CAP_EDGE",EDGE,{"disambiguationData":[OSD([sQuery(id+"F0.wireOp",EDGE,"E32")])],"isStart":true});
            var Q22;
            Q22=makeQuery(id+"F1.opExtrude","CAP_EDGE",EDGE,{"disambiguationData":[OSD([sQuery(id+"F0.wireOp",EDGE,"E23.0")])],"isStart":true});
            var Q23;
            Q23=makeQuery(id+"F1.opExtrude","CAP_EDGE",EDGE,{"disambiguationData":[OSD([sQuery(id+"F0.wireOp",EDGE,"E16.0")])],"isStart":true});
            fillet(context, id + "F3", {"entities" : qUnion([Q0, Q1, Q2, Q3, Q4, Q5, Q6, Q7, Q8, Q9, Q10, Q11, Q12, Q13, Q14, Q15, Q16, Q17, Q18, Q19, Q20, Q21, Q22, Q23]), "radius" : 3.5 * mm, "tangentPropagation" : true, "allowEdgeOverflow" : false});
        }
        {
            var Q0;
            Q0=makeQuery(id+"F1.opExtrude","CAP_EDGE",EDGE,{"disambiguationData":[OSD([sQuery(id+"F0.wireOp",EDGE,"E27")])],"isStart":false});
            var Q1;
            Q1=makeQuery(id+"F1.opExtrude","CAP_EDGE",EDGE,{"disambiguationData":[OSD([sQuery(id+"F0.wireOp",EDGE,"E25")])],"isStart":false});
            var Q2;
            Q2=makeQuery(id+"F1.opExtrude","CAP_EDGE",EDGE,{"disambiguationData":[OSD([sQuery(id+"F0.wireOp",EDGE,"E10")])],"isStart":false});
            var Q3;
            Q3=makeQuery(id+"F1.opExtrude","CAP_EDGE",EDGE,{"disambiguationData":[OSD([sQuery(id+"F0.wireOp",EDGE,"E26")])],"isStart":false});
            var Q4;
            Q4=makeQuery(id+"F1.opExtrude","CAP_EDGE",EDGE,{"disambiguationData":[OSD([sQuery(id+"F0.wireOp",EDGE,"E27")])],"isStart":true});
            var Q5;
            Q5=makeQuery(id+"F1.opExtrude","CAP_EDGE",EDGE,{"disambiguationData":[OSD([sQuery(id+"F0.wireOp",EDGE,"E10")])],"isStart":true});
            var Q6;
            Q6=makeQuery(id+"F1.opExtrude","CAP_EDGE",EDGE,{"disambiguationData":[OSD([sQuery(id+"F0.wireOp",EDGE,"E26")])],"isStart":true});
            var Q7;
            Q7=makeQuery(id+"F1.opExtrude","CAP_EDGE",EDGE,{"disambiguationData":[OSD([sQuery(id+"F0.wireOp",EDGE,"E25")])],"isStart":true});
            fillet(context, id + "F4", {"entities" : qUnion([Q0, Q1, Q2, Q3, Q4, Q5, Q6, Q7]), "radius" : 2 * mm, "tangentPropagation" : true, "allowEdgeOverflow" : false});
        }
    });
